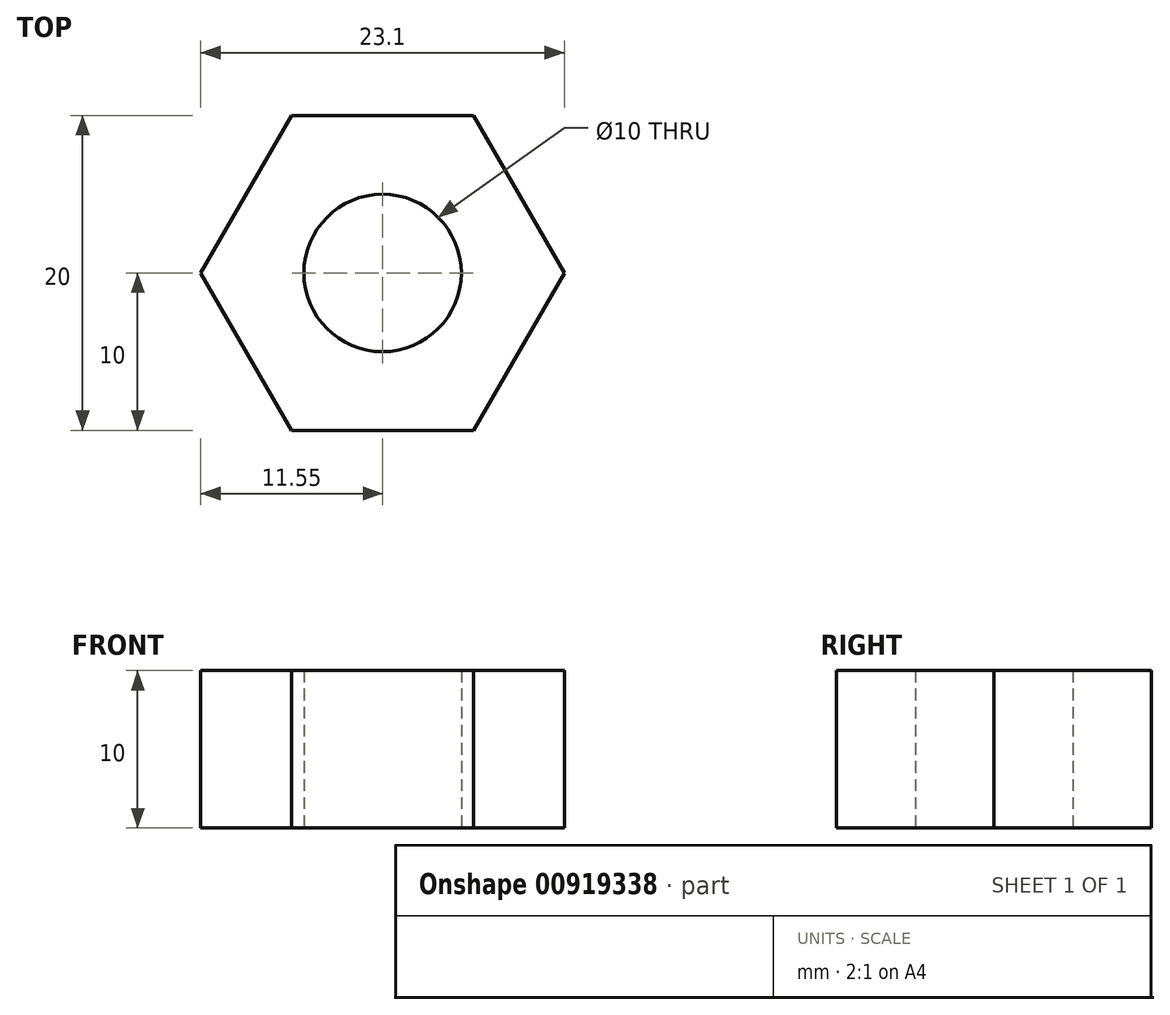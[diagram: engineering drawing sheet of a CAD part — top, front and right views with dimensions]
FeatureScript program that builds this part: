
annotation { "Feature Type Name" : "Feature", "Feature Type Description" : "" }
export const myFeature = defineFeature(function(context is Context, id is Id, definition is map)
    precondition{}
    {
        {
            var Q0;
            Q0=qCreatedBy(makeId("Top.planeOp"),FACE);
            var sketch = newSketch(context, id + "F0", { "sketchPlane" : qUnion([Q0])});
            skCircle(sketch, "E0", {"center": v(0, 0) * mm, "radius": 5 * mm});
            skCircle(sketch, "E1.cCircle", {"center": v(0, 0) * mm, "radius": 10 * mm, "construction": true});
            skLineSegment(sketch, "E1.0", {"start": v(5.77, -10) * mm, "end": v(-5.77, -10) * mm});
            skLineSegment(sketch, "E1.1", {"start": v(-5.77, -10) * mm, "end": v(-11.55, 0) * mm});
            skLineSegment(sketch, "E1.2", {"start": v(-11.55, 0) * mm, "end": v(-5.77, 10) * mm});
            skLineSegment(sketch, "E1.3", {"start": v(-5.77, 10) * mm, "end": v(5.77, 10) * mm});
            skLineSegment(sketch, "E1.4", {"start": v(5.77, 10) * mm, "end": v(11.55, 0) * mm});
            skLineSegment(sketch, "E1.5", {"start": v(11.55, 0) * mm, "end": v(5.77, -10) * mm});
            skPoint(sketch, "E1.0.midPoint", {"position": v(0, -10) * mm});
            skSolve(sketch);
        }
        {
            var Q0;
            Q0 = qSketchRegion(id + "F0", true);
            extrude(context, id + "F1", {"entities" : qUnion([Q0]), "depth" : 10 * mm, "offsetDistance" : 25 * mm});
        }
    });
